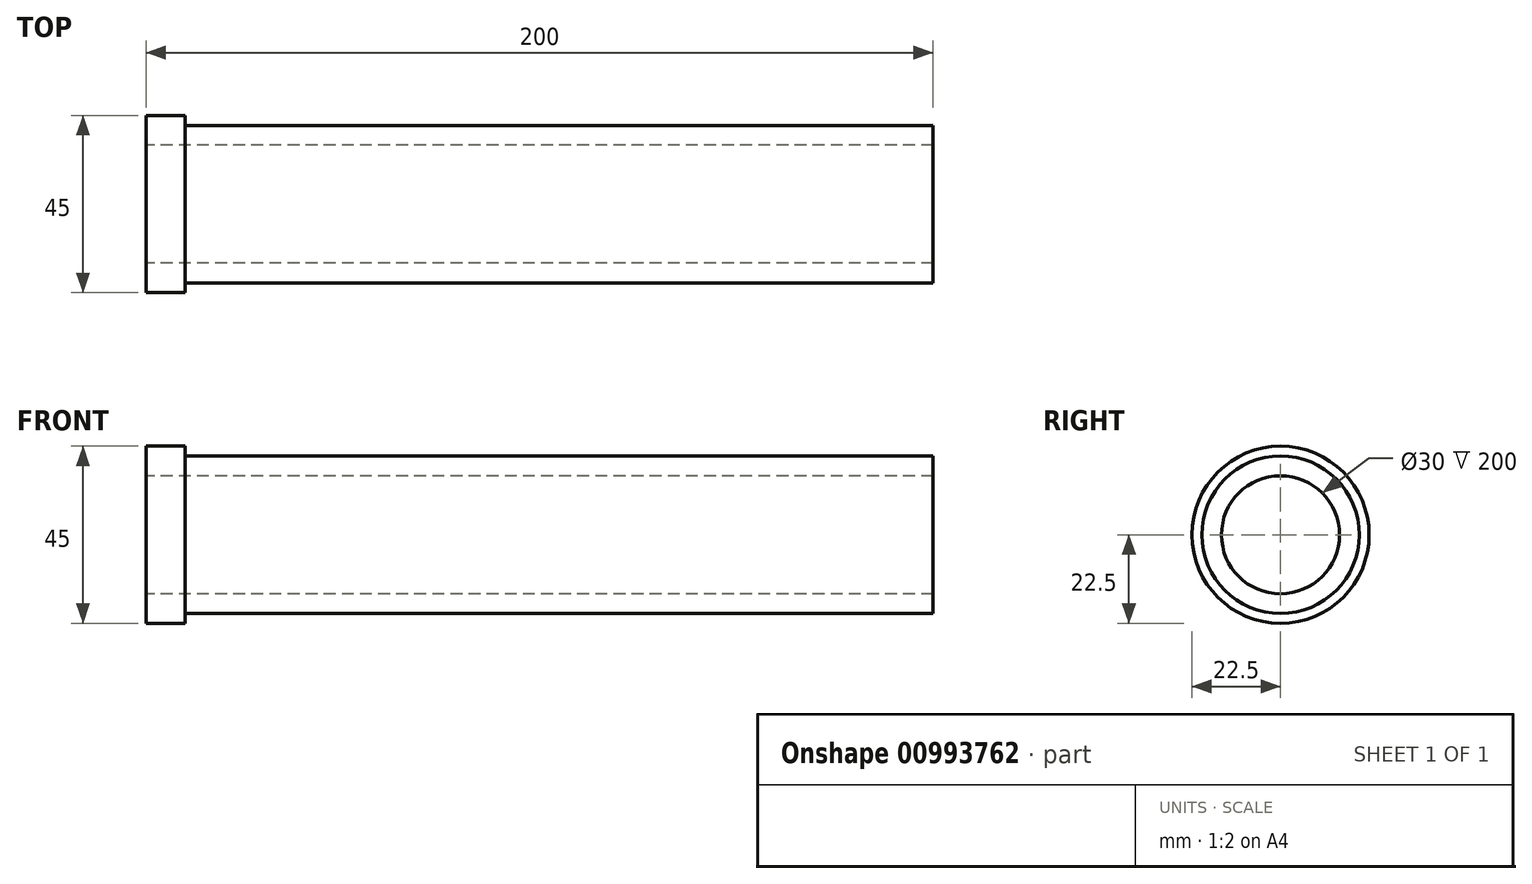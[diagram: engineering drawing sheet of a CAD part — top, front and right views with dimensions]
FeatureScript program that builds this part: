
annotation { "Feature Type Name" : "Feature", "Feature Type Description" : "" }
export const myFeature = defineFeature(function(context is Context, id is Id, definition is map)
    precondition{}
    {
        {
            var Q0;
            Q0=qCreatedBy(makeId("Right.planeOp"),FACE);
            var sketch = newSketch(context, id + "F0", { "sketchPlane" : qUnion([Q0])});
            skCircle(sketch, "E0", {"center": v(0, 0) * mm, "radius": 20 * mm});
            skCircle(sketch, "E1", {"center": v(0, 0) * mm, "radius": 15 * mm});
            skSolve(sketch);
        }
        {
            var Q0;
            Q0 = qSketchRegion(id + "F0", true);
            extrude(context, id + "F1", {"entities" : qUnion([Q0]), "endBound" : BoundingType.SYMMETRIC, "depth" : 200 * mm, "offsetDistance" : 25 * mm});
        }
        {
            var Q0;
            Q0=makeQuery(id+"F1.opExtrude","CAP_FACE",FACE,{"disambiguationData":[OSD([sQuery(id+"F0.wireOp",EDGE,"E0"),sQuery(id+"F0.wireOp",EDGE,"E1")])],"isStart":true});
            var sketch = newSketch(context, id + "F2", { "sketchPlane" : qUnion([Q0])});
            skCircle(sketch, "E2", {"center": v(0, 0) * mm, "radius": 22.5 * mm});
            skCircle(sketch, "E3", {"center": v(0, 0) * mm, "radius": 20 * mm});
            skSolve(sketch);
        }
        {
            var Q0;
            Q0=makeQuery(id+"F2.imprint","IMPRINT",FACE,{"disambiguationData":[TD([[makeQuery(id+"F2.imprint","IMPRINT",EDGE,{"derivedFrom":sQuery(id+"F2.wireOp",EDGE,"E2")}),1.0]])]});
            extrude(context, id + "F3", {"entities" : qUnion([Q0]), "operationType" : NewBodyOperationType.ADD, "oppositeDirection" : true, "depth" : 10 * mm, "offsetDistance" : 25 * mm});
        }
    });
